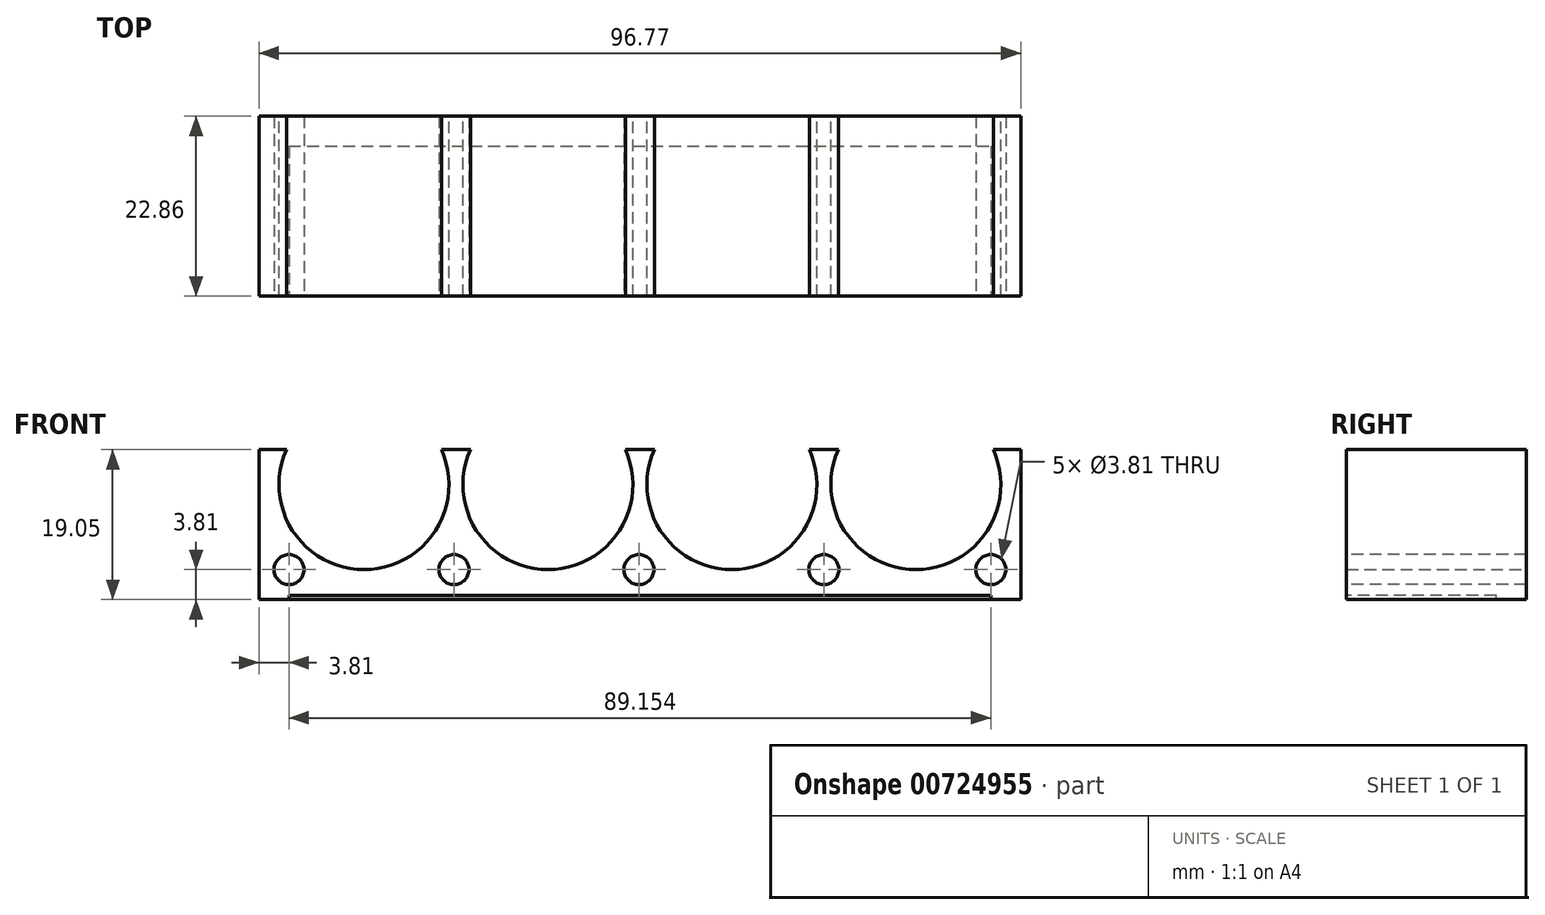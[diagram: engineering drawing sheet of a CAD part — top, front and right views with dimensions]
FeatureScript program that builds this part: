
annotation { "Feature Type Name" : "Feature", "Feature Type Description" : "" }
export const myFeature = defineFeature(function(context is Context, id is Id, definition is map)
    precondition{}
    {
        {
            var Q0;
            Q0=qCreatedBy(makeId("Front.planeOp"),FACE);
            var sketch = newSketch(context, id + "F0", { "sketchPlane" : qUnion([Q0])});
            skLineSegment(sketch, "E0", {"start": v(0, 0) * mm, "end": v(96.77, 0) * mm});
            skLineSegment(sketch, "E1", {"start": v(96.77, 0) * mm, "end": v(96.77, 19.05) * mm});
            skLineSegment(sketch, "E2", {"start": v(96.77, 19.05) * mm, "end": v(93.28, 19.05) * mm});
            skLineSegment(sketch, "E3", {"start": v(0, 19.05) * mm, "end": v(0, 0) * mm});
            skArc(sketch, "E4", {"start": v(3.5, 19.05) * mm, "mid": v(13.34, 3.8) * mm, "end": v(23.17, 19.05) * mm});
            skArc(sketch, "E5", {"start": v(26.87, 19.05) * mm, "mid": v(36.7, 3.8) * mm, "end": v(46.54, 19.05) * mm});
            skArc(sketch, "E6", {"start": v(50.23, 19.05) * mm, "mid": v(60.07, 3.8) * mm, "end": v(69.9, 19.05) * mm});
            skArc(sketch, "E7", {"start": v(73.6, 19.05) * mm, "mid": v(83.44, 3.81) * mm, "end": v(93.28, 19.05) * mm});
            skLineSegment(sketch, "E8.trimOffspring", {"start": v(3.5, 19.05) * mm, "end": v(0, 19.05) * mm});
            skLineSegment(sketch, "E9.trimOffspring", {"start": v(26.87, 19.05) * mm, "end": v(23.17, 19.05) * mm});
            skLineSegment(sketch, "E10.trimOffspring", {"start": v(50.23, 19.05) * mm, "end": v(46.54, 19.05) * mm});
            skLineSegment(sketch, "E11", {"start": v(69.9, 19.05) * mm, "end": v(73.6, 19.05) * mm});
            skSolve(sketch);
        }
        {
            var Q0;
            Q0=makeQuery(id+"F0.imprint","IMPRINT",FACE,{"disambiguationData":[TD([[makeQuery(id+"F0.imprint","IMPRINT",EDGE,{"derivedFrom":sQuery(id+"F0.wireOp",EDGE,"E0")}),1.0]])]});
            extrude(context, id + "F1", {"entities" : qUnion([Q0]), "depth" : 22.86 * mm, "offsetDistance" : 25.4 * mm});
        }
        {
            var Q0;
            Q0=makeQuery(id+"F1.opExtrude","CAP_FACE",FACE,{"disambiguationData":[OSD([sQuery(id+"F0.wireOp",EDGE,"E0"),sQuery(id+"F0.wireOp",EDGE,"E1"),sQuery(id+"F0.wireOp",EDGE,"E2"),sQuery(id+"F0.wireOp",EDGE,"E3"),sQuery(id+"F0.wireOp",EDGE,"E4"),sQuery(id+"F0.wireOp",EDGE,"E5"),sQuery(id+"F0.wireOp",EDGE,"E6"),sQuery(id+"F0.wireOp",EDGE,"E7"),sQuery(id+"F0.wireOp",EDGE,"E8.trimOffspring"),sQuery(id+"F0.wireOp",EDGE,"E9.trimOffspring"),sQuery(id+"F0.wireOp",EDGE,"E10.trimOffspring"),sQuery(id+"F0.wireOp",EDGE,"E11")])],"isStart":false});
            var sketch = newSketch(context, id + "F2", { "sketchPlane" : qUnion([Q0])});
            skCircle(sketch, "E12", {"center": v(24.77, 3.8) * mm, "radius": 1.9 * mm});
            skCircle(sketch, "E13", {"center": v(48.26, 3.81) * mm, "radius": 1.9 * mm});
            skCircle(sketch, "E14", {"center": v(71.76, 3.81) * mm, "radius": 1.9 * mm});
            skCircle(sketch, "E15", {"center": v(3.81, 3.8) * mm, "radius": 1.9 * mm});
            skCircle(sketch, "E16", {"center": v(92.96, 3.81) * mm, "radius": 1.9 * mm});
            skSolve(sketch);
        }
        {
            var Q0;
            Q0 = qSketchRegion(id + "F2", true);
            extrude(context, id + "F3", {"entities" : qUnion([Q0]), "operationType" : NewBodyOperationType.REMOVE, "oppositeDirection" : true, "depth" : 50.8 * mm, "offsetDistance" : 25.4 * mm});
        }
        {
            var Q0;
            Q0=makeQuery(id+"F1.opExtrude","CAP_FACE",FACE,{"disambiguationData":[OSD([sQuery(id+"F0.wireOp",EDGE,"E0"),sQuery(id+"F0.wireOp",EDGE,"E1"),sQuery(id+"F0.wireOp",EDGE,"E2"),sQuery(id+"F0.wireOp",EDGE,"E3"),sQuery(id+"F0.wireOp",EDGE,"E4"),sQuery(id+"F0.wireOp",EDGE,"E5"),sQuery(id+"F0.wireOp",EDGE,"E6"),sQuery(id+"F0.wireOp",EDGE,"E7"),sQuery(id+"F0.wireOp",EDGE,"E8.trimOffspring"),sQuery(id+"F0.wireOp",EDGE,"E9.trimOffspring"),sQuery(id+"F0.wireOp",EDGE,"E10.trimOffspring"),sQuery(id+"F0.wireOp",EDGE,"E11")])],"isStart":false});
            var sketch = newSketch(context, id + "F4", { "sketchPlane" : qUnion([Q0])});
            skLineSegment(sketch, "E17", {"start": v(3.81, 0) * mm, "end": v(3.81, 0.5) * mm});
            skLineSegment(sketch, "E18", {"start": v(3.81, 0.5) * mm, "end": v(92.96, 0.5) * mm});
            skLineSegment(sketch, "E19", {"start": v(92.96, 0.5) * mm, "end": v(92.96, 0) * mm});
            skLineSegment(sketch, "E20", {"start": v(92.96, 0) * mm, "end": v(3.81, 0) * mm});
            skSolve(sketch);
        }
        {
            var Q0;
            Q0 = qSketchRegion(id + "F4", true);
            extrude(context, id + "F5", {"entities" : qUnion([Q0]), "operationType" : NewBodyOperationType.REMOVE, "oppositeDirection" : true, "depth" : 19.05 * mm, "offsetDistance" : 25.4 * mm});
        }
    });
